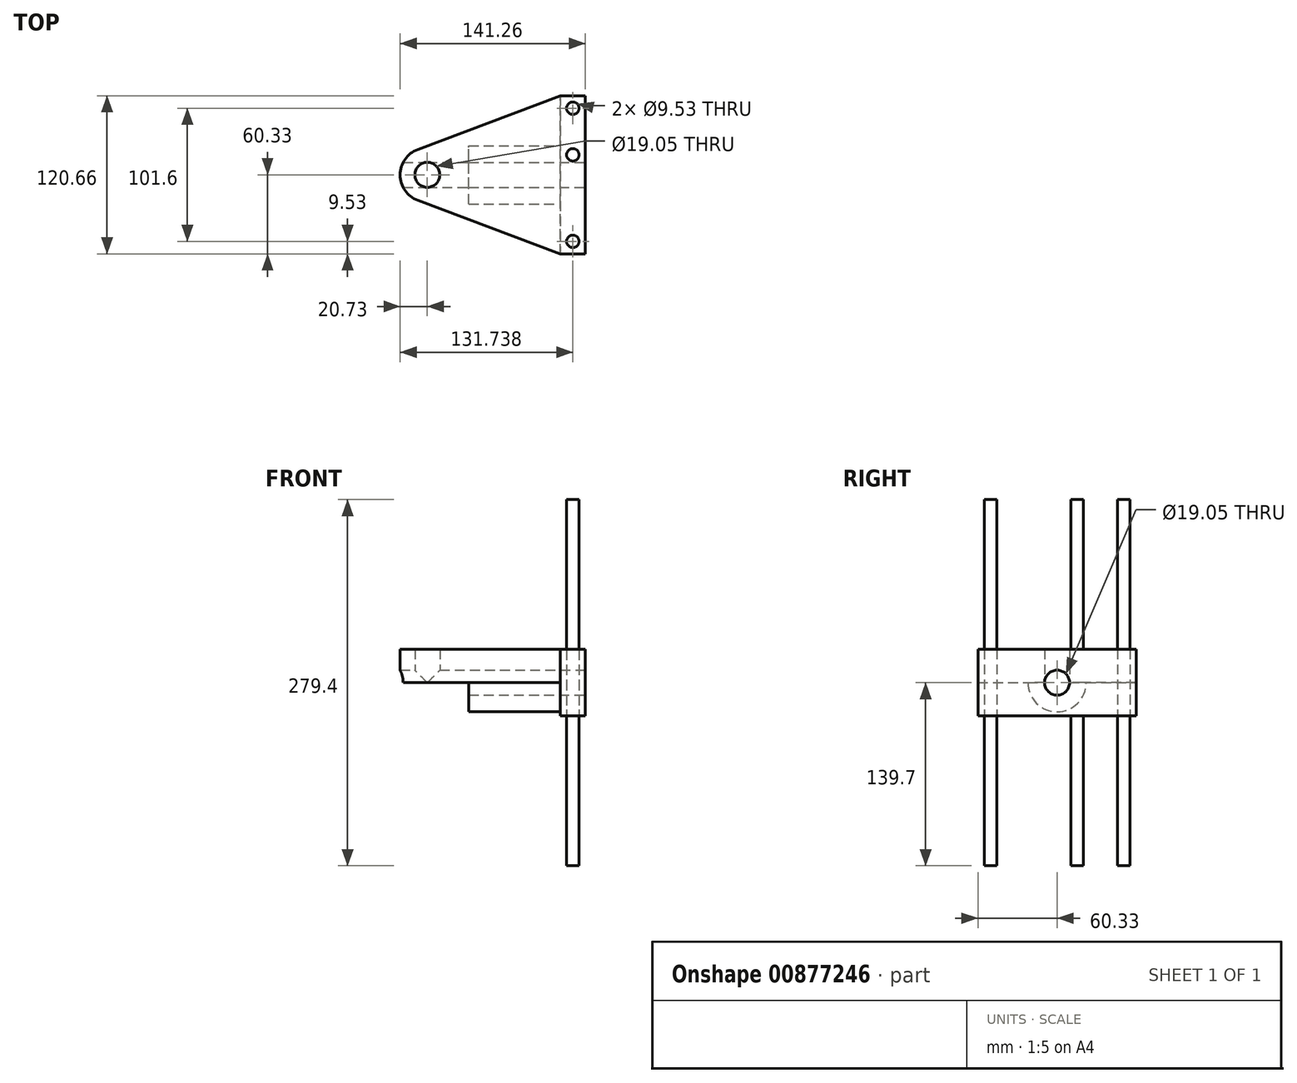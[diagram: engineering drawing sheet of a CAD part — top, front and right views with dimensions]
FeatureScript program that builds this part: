
annotation { "Feature Type Name" : "Feature", "Feature Type Description" : "" }
export const myFeature = defineFeature(function(context is Context, id is Id, definition is map)
    precondition{}
    {
        {
            var Q0;
            Q0=qCreatedBy(makeId("Top.planeOp"),FACE);
            var sketch = newSketch(context, id + "F0", { "sketchPlane" : qUnion([Q0])});
            skCircle(sketch, "E0", {"center": v(111, 50.8) * mm, "radius": 4.76 * mm});
            skCircle(sketch, "E1", {"center": v(111, -50.8) * mm, "radius": 4.76 * mm});
            skCircle(sketch, "E2", {"center": v(111, 15.24) * mm, "radius": 4.76 * mm});
            skLineSegment(sketch, "E3.bottom", {"start": v(120.53, 60.33) * mm, "end": v(101.48, 60.33) * mm});
            skLineSegment(sketch, "E3.top", {"start": v(120.53, -60.32) * mm, "end": v(101.48, -60.32) * mm});
            skLineSegment(sketch, "E3.left", {"start": v(120.53, 60.32) * mm, "end": v(120.53, -60.32) * mm});
            skLineSegment(sketch, "E3.right", {"start": v(101.48, 60.32) * mm, "end": v(101.48, -60.32) * mm});
            skLineSegment(sketch, "E4", {"start": v(101.48, 60.33) * mm, "end": v(-7.3, 19.4) * mm});
            skLineSegment(sketch, "E5", {"start": v(101.48, -60.33) * mm, "end": v(-7.3, -19.4) * mm});
            skArc(sketch, "E6", {"start": v(-7.3, 19.4) * mm, "mid": v(-20.73, 0) * mm, "end": v(-7.3, -19.4) * mm});
            skCircle(sketch, "E7", {"center": v(0, 0) * mm, "radius": 9.53 * mm});
            skLineSegment(sketch, "E8", {"start": v(111, 60.32) * mm, "end": v(111, -60.32) * mm, "construction": true});
            skPoint(sketch, "E9", {"position": v(111, 60.32) * mm});
            skPoint(sketch, "E10", {"position": v(111, -60.32) * mm});
            skSolve(sketch);
        }
        {
            var Q0;
            Q0=makeQuery(id+"F0.imprint","IMPRINT",FACE,{"disambiguationData":[TD([[makeQuery(id+"F0.imprint","IMPRINT",EDGE,{"derivedFrom":sQuery(id+"F0.wireOp",EDGE,"E0")}),1.0]])]});
            var Q1;
            Q1=makeQuery(id+"F0.imprint","IMPRINT",FACE,{"disambiguationData":[TD([[makeQuery(id+"F0.imprint","IMPRINT",EDGE,{"derivedFrom":sQuery(id+"F0.wireOp",EDGE,"E2")}),1.0]])]});
            var Q2;
            Q2=makeQuery(id+"F0.imprint","IMPRINT",FACE,{"disambiguationData":[TD([[makeQuery(id+"F0.imprint","IMPRINT",EDGE,{"derivedFrom":sQuery(id+"F0.wireOp",EDGE,"E1")}),1.0]])]});
            var Q3;
            Q3=sQuery(id+"F0.wireOp",EDGE,"E0");
            var Q4;
            Q4=sQuery(id+"F0.wireOp",EDGE,"E2");
            var Q5;
            Q5=sQuery(id+"F0.wireOp",EDGE,"E1");
            extrude(context, id + "F1", {"entities" : qUnion([Q0, Q1, Q2]), "surfaceEntities" : qUnion([Q3, Q4, Q5]), "depth" : 279.4 * mm, "offsetDistance" : 25.4 * mm, "symmetric" : true});
        }
        {
            var Q0;
            Q0 = qSketchRegion(id + "F0", true);
            extrude(context, id + "F2", {"entities" : qUnion([Q0]), "depth" : 25.4 * mm, "offsetDistance" : 25.4 * mm});
        }
        {
            var Q0;
            Q0=makeQuery(id+"F0.imprint","IMPRINT",FACE,{"disambiguationData":[TD([[makeQuery(id+"F0.imprint","IMPRINT",EDGE,{"derivedFrom":sQuery(id+"F0.wireOp",EDGE,"E0")}),-1.0]])]});
            extrude(context, id + "F3", {"entities" : qUnion([Q0]), "depth" : 50.8 * mm, "offsetDistance" : 25.4 * mm, "symmetric" : true});
        }
        {
            var Q0;
            Q0=makeQuery(id+"F3.opExtrude","SWEPT_FACE",FACE,{"disambiguationData":[OSD([sQuery(id+"F0.wireOp",EDGE,"E3.left")])]});
            var sketch = newSketch(context, id + "F4", { "sketchPlane" : qUnion([Q0])});
            skCircle(sketch, "E11", {"center": v(0, 0) * mm, "radius": 9.53 * mm});
            skCircle(sketch, "E12", {"center": v(0, 0) * mm, "radius": 22.23 * mm});
            skSolve(sketch);
        }
        {
            var Q0;
            Q0=makeQuery(id+"F4.imprint","IMPRINT",FACE,{"disambiguationData":[TD([[makeQuery(id+"F4.imprint","IMPRINT",EDGE,{"derivedFrom":sQuery(id+"F4.wireOp",EDGE,"E11")}),-1.0]])]});
            extrude(context, id + "F5", {"entities" : qUnion([Q0]), "operationType" : NewBodyOperationType.ADD, "oppositeDirection" : true, "depth" : 88.9 * mm, "offsetDistance" : 25.4 * mm});
        }
        {
            var Q0;
            Q0=makeQuery(id+"F4.imprint","IMPRINT",FACE,{"disambiguationData":[TD([[makeQuery(id+"F4.imprint","IMPRINT",EDGE,{"derivedFrom":sQuery(id+"F4.wireOp",EDGE,"E11")}),1.0]])]});
            extrude(context, id + "F6", {"entities" : qUnion([Q0]), "operationType" : NewBodyOperationType.REMOVE, "endBound" : BoundingType.THROUGH_ALL, "oppositeDirection" : true, "depth" : 25.4 * mm, "offsetDistance" : 25.4 * mm});
        }
    });
